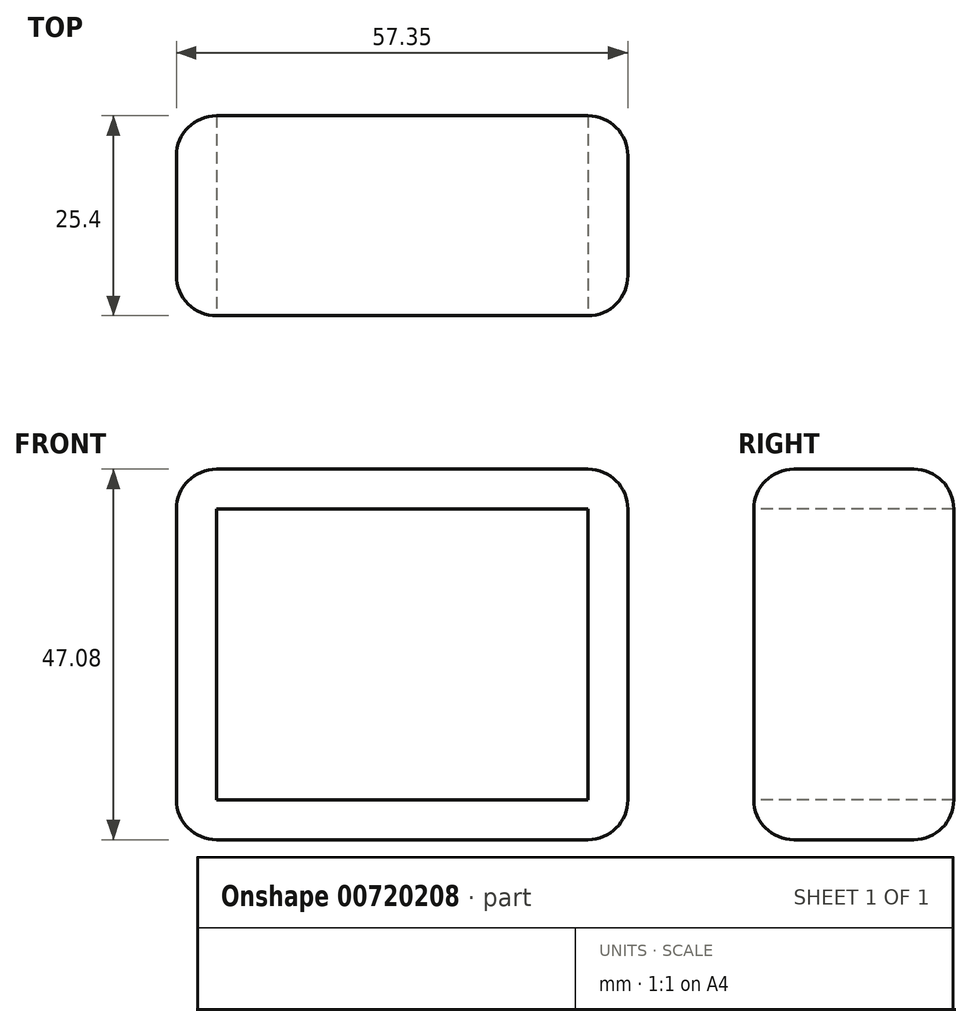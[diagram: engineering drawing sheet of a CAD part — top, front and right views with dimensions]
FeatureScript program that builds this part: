
annotation { "Feature Type Name" : "Feature", "Feature Type Description" : "" }
export const myFeature = defineFeature(function(context is Context, id is Id, definition is map)
    precondition{}
    {
        {
            var Q0;
            Q0=qCreatedBy(makeId("Front.planeOp"),FACE);
            var sketch = newSketch(context, id + "F0", { "sketchPlane" : qUnion([Q0])});
            skLineSegment(sketch, "E0.bottom", {"start": v(-30.18, -23.04) * mm, "end": v(27.17, -23.04) * mm});
            skLineSegment(sketch, "E0.top", {"start": v(-30.18, 24.04) * mm, "end": v(27.17, 24.04) * mm});
            skLineSegment(sketch, "E0.left", {"start": v(-30.18, -23.04) * mm, "end": v(-30.18, 24.04) * mm});
            skLineSegment(sketch, "E0.right", {"start": v(27.17, -23.04) * mm, "end": v(27.17, 24.04) * mm});
            skSolve(sketch);
        }
        {
            var Q0;
            Q0 = qSketchRegion(id + "F0", true);
            extrude(context, id + "F1", {"entities" : qUnion([Q0]), "depth" : 25.4 * mm, "offsetDistance" : 25.4 * mm});
        }
        {
            var Q0;
            Q0=makeQuery(id+"F1.opExtrude","CAP_FACE",FACE,{"disambiguationData":[OSD([sQuery(id+"F0.wireOp",EDGE,"E0.bottom"),sQuery(id+"F0.wireOp",EDGE,"E0.top"),sQuery(id+"F0.wireOp",EDGE,"E0.left"),sQuery(id+"F0.wireOp",EDGE,"E0.right")])],"isStart":false});
            fillet(context, id + "F2", {"entities" : qUnion([Q0]), "tangentPropagation" : true, "radius" : 5.08 * mm, "defaultsChanged" : false, "vertexSettings" : [], "allowEdgeOverflow" : false});
        }
        {
            var Q0;
            Q0=makeQuery(id+"F1.opExtrude","SWEPT_EDGE",EDGE,{"disambiguationData":[OSD([sQuery(id+"F0.wireOp",EDGE,"E0.top"),sQuery(id+"F0.wireOp",EDGE,"E0.right")])]});
            var Q1;
            Q1=makeQuery(id+"F1.opExtrude","CAP_EDGE",EDGE,{"disambiguationData":[OSD([sQuery(id+"F0.wireOp",EDGE,"E0.right")])],"isStart":true});
            var Q2;
            Q2=makeQuery(id+"F1.opExtrude","SWEPT_EDGE",EDGE,{"disambiguationData":[OSD([sQuery(id+"F0.wireOp",EDGE,"E0.bottom"),sQuery(id+"F0.wireOp",EDGE,"E0.right")])]});
            fillet(context, id + "F3", {"entities" : qUnion([Q0, Q1, Q2]), "tangentPropagation" : true, "radius" : 5.08 * mm, "defaultsChanged" : false, "vertexSettings" : [], "allowEdgeOverflow" : false});
        }
        {
            var Q0;
            Q0=makeQuery(id+"F1.opExtrude","CAP_EDGE",EDGE,{"disambiguationData":[OSD([sQuery(id+"F0.wireOp",EDGE,"E0.bottom")])],"isStart":true});
            var Q1;
            Q1=makeQuery(id+"F1.opExtrude","SWEPT_EDGE",EDGE,{"disambiguationData":[OSD([sQuery(id+"F0.wireOp",EDGE,"E0.bottom"),sQuery(id+"F0.wireOp",EDGE,"E0.left")])]});
            var Q2;
            Q2=makeQuery(id+"F1.opExtrude","CAP_EDGE",EDGE,{"disambiguationData":[OSD([sQuery(id+"F0.wireOp",EDGE,"E0.left")])],"isStart":true});
            fillet(context, id + "F4", {"entities" : qUnion([Q0, Q1, Q2]), "tangentPropagation" : true, "radius" : 5.08 * mm, "defaultsChanged" : false, "vertexSettings" : [], "allowEdgeOverflow" : false});
        }
        {
            var Q0;
            Q0=makeQuery(id+"F1.opExtrude","CAP_EDGE",EDGE,{"disambiguationData":[OSD([sQuery(id+"F0.wireOp",EDGE,"E0.top")])],"isStart":true});
            var Q1;
            Q1=makeQuery(id+"F1.opExtrude","SWEPT_EDGE",EDGE,{"disambiguationData":[OSD([sQuery(id+"F0.wireOp",EDGE,"E0.top"),sQuery(id+"F0.wireOp",EDGE,"E0.left")])]});
            fillet(context, id + "F5", {"entities" : qUnion([Q0, Q1]), "tangentPropagation" : true, "radius" : 5.08 * mm, "defaultsChanged" : false, "vertexSettings" : [], "allowEdgeOverflow" : false});
        }
        {
            var Q0;
            Q0=makeQuery(id+"F1.opExtrude","CAP_FACE",FACE,{"disambiguationData":[OSD([sQuery(id+"F0.wireOp",EDGE,"E0.bottom"),sQuery(id+"F0.wireOp",EDGE,"E0.top"),sQuery(id+"F0.wireOp",EDGE,"E0.left"),sQuery(id+"F0.wireOp",EDGE,"E0.right")])],"isStart":false});
            extrude(context, id + "F6", {"entities" : qUnion([Q0]), "operationType" : NewBodyOperationType.REMOVE, "oppositeDirection" : true, "depth" : 25.4 * mm, "offsetDistance" : 25.4 * mm});
        }
    });
